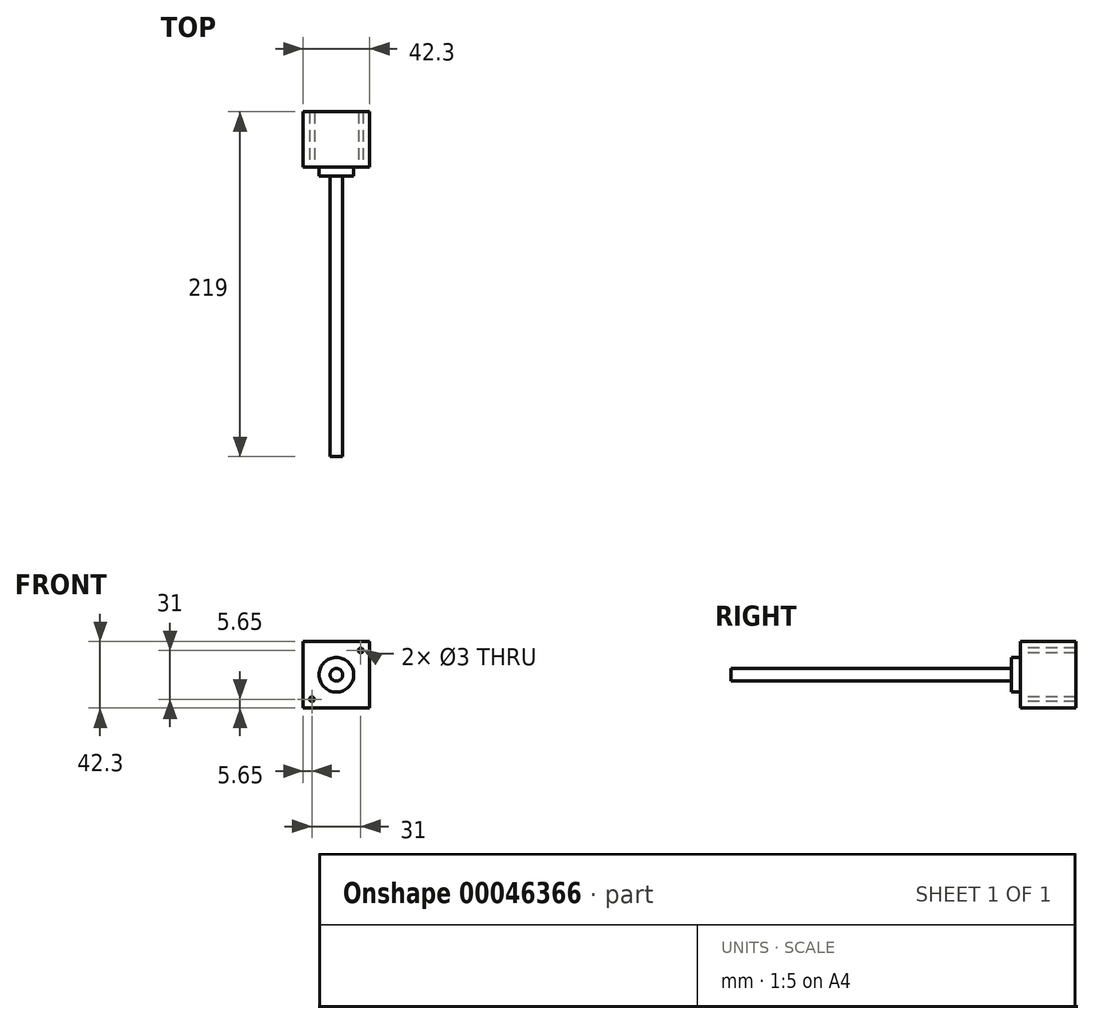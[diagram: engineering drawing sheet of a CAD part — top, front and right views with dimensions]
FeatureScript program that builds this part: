
annotation { "Feature Type Name" : "Feature", "Feature Type Description" : "" }
export const myFeature = defineFeature(function(context is Context, id is Id, definition is map)
    precondition{}
    {
        {
            var Q0;
            Q0=qCreatedBy(makeId("Front.planeOp"),FACE);
            var sketch = newSketch(context, id + "F0", { "sketchPlane" : qUnion([Q0])});
            skLineSegment(sketch, "E0.bottom", {"start": v(0, 0) * mm, "end": v(42.3, 0) * mm});
            skLineSegment(sketch, "E0.top", {"start": v(0, 42.3) * mm, "end": v(42.3, 42.3) * mm});
            skLineSegment(sketch, "E0.left", {"start": v(0, 0) * mm, "end": v(0, 42.3) * mm});
            skLineSegment(sketch, "E0.right", {"start": v(42.3, 0) * mm, "end": v(42.3, 42.3) * mm});
            skLineSegment(sketch, "E1", {"start": v(0, 21.15) * mm, "end": v(42.3, 21.15) * mm, "construction": true});
            skLineSegment(sketch, "E2", {"start": v(21.15, 42.3) * mm, "end": v(21.15, 0) * mm, "construction": true});
            skCircle(sketch, "E3", {"center": v(21.15, 21.15) * mm, "radius": 11 * mm});
            skCircle(sketch, "E4", {"center": v(5.65, 36.65) * mm, "radius": 1.5 * mm});
            skCircle(sketch, "E5.0.MirrorC", {"center": v(36.65, 36.65) * mm, "radius": 1.5 * mm});
            skCircle(sketch, "E6.0.MirrorC", {"center": v(5.65, 5.65) * mm, "radius": 1.5 * mm});
            skCircle(sketch, "E7.0.MirrorC", {"center": v(36.65, 5.65) * mm, "radius": 1.5 * mm});
            skCircle(sketch, "E8", {"center": v(21.15, 21.15) * mm, "radius": 4 * mm});
            skCircle(sketch, "E9", {"center": v(21.15, 21.15) * mm, "radius": 2.5 * mm});
            skSolve(sketch);
        }
        {
            var Q0;
            Q0=makeQuery(id+"F0.imprint","IMPRINT",FACE,{"disambiguationData":[TD([[makeQuery(id+"F0.imprint","IMPRINT",EDGE,{"derivedFrom":sQuery(id+"F0.wireOp",EDGE,"E0.bottom")}),1.0]])]});
            var Q1;
            Q1=makeQuery(id+"F0.imprint","IMPRINT",FACE,{"disambiguationData":[TD([[makeQuery(id+"F0.imprint","IMPRINT",EDGE,{"derivedFrom":sQuery(id+"F0.wireOp",EDGE,"E4")}),1.0]])]});
            var Q2;
            Q2=makeQuery(id+"F0.imprint","IMPRINT",FACE,{"disambiguationData":[TD([[makeQuery(id+"F0.imprint","IMPRINT",EDGE,{"derivedFrom":sQuery(id+"F0.wireOp",EDGE,"E5.0.MirrorC")}),-1.0]])]});
            var Q3;
            Q3=makeQuery(id+"F0.imprint","IMPRINT",FACE,{"disambiguationData":[TD([[makeQuery(id+"F0.imprint","IMPRINT",EDGE,{"derivedFrom":sQuery(id+"F0.wireOp",EDGE,"E3")}),1.0]])]});
            var Q4;
            Q4=makeQuery(id+"F0.imprint","IMPRINT",FACE,{"disambiguationData":[TD([[makeQuery(id+"F0.imprint","IMPRINT",EDGE,{"derivedFrom":sQuery(id+"F0.wireOp",EDGE,"E6.0.MirrorC")}),-1.0]])]});
            var Q5;
            Q5=makeQuery(id+"F0.imprint","IMPRINT",FACE,{"disambiguationData":[TD([[makeQuery(id+"F0.imprint","IMPRINT",EDGE,{"derivedFrom":sQuery(id+"F0.wireOp",EDGE,"E7.0.MirrorC")}),1.0]])]});
            var Q6;
            Q6=makeQuery(id+"F0.imprint","IMPRINT",FACE,{"disambiguationData":[TD([[makeQuery(id+"F0.imprint","IMPRINT",EDGE,{"derivedFrom":sQuery(id+"F0.wireOp",EDGE,"E8")}),1.0]])]});
            var Q7;
            Q7=makeQuery(id+"F0.imprint","IMPRINT",FACE,{"disambiguationData":[TD([[makeQuery(id+"F0.imprint","IMPRINT",EDGE,{"derivedFrom":sQuery(id+"F0.wireOp",EDGE,"E9")}),1.0]])]});
            extrude(context, id + "F1", {"entities" : qUnion([Q0, Q1, Q2, Q3, Q4, Q5, Q6, Q7]), "oppositeDirection" : true, "depth" : 39 * mm});
        }
        {
            var Q0;
            Q0=makeQuery(id+"F0.imprint","IMPRINT",FACE,{"disambiguationData":[TD([[makeQuery(id+"F0.imprint","IMPRINT",EDGE,{"derivedFrom":sQuery(id+"F0.wireOp",EDGE,"E3")}),1.0]])]});
            var Q1;
            Q1=makeQuery(id+"F0.imprint","IMPRINT",FACE,{"disambiguationData":[TD([[makeQuery(id+"F0.imprint","IMPRINT",EDGE,{"derivedFrom":sQuery(id+"F0.wireOp",EDGE,"E9")}),1.0]])]});
            var Q2;
            Q2=makeQuery(id+"F0.imprint","IMPRINT",FACE,{"disambiguationData":[TD([[makeQuery(id+"F0.imprint","IMPRINT",EDGE,{"derivedFrom":sQuery(id+"F0.wireOp",EDGE,"E8")}),1.0]])]});
            extrude(context, id + "F2", {"entities" : qUnion([Q0, Q1, Q2]), "operationType" : NewBodyOperationType.ADD, "depth" : 2 * mm});
        }
        {
            var Q0;
            Q0=makeQuery(id+"F0.imprint","IMPRINT",FACE,{"disambiguationData":[TD([[makeQuery(id+"F0.imprint","IMPRINT",EDGE,{"derivedFrom":sQuery(id+"F0.wireOp",EDGE,"E4")}),1.0]])]});
            var Q1;
            Q1=makeQuery(id+"F0.imprint","IMPRINT",FACE,{"disambiguationData":[TD([[makeQuery(id+"F0.imprint","IMPRINT",EDGE,{"derivedFrom":sQuery(id+"F0.wireOp",EDGE,"E5.0.MirrorC")}),-1.0]])]});
            var Q2;
            Q2=makeQuery(id+"F0.imprint","IMPRINT",FACE,{"disambiguationData":[TD([[makeQuery(id+"F0.imprint","IMPRINT",EDGE,{"derivedFrom":sQuery(id+"F0.wireOp",EDGE,"E7.0.MirrorC")}),1.0]])]});
            var Q3;
            Q3=makeQuery(id+"F0.imprint","IMPRINT",FACE,{"disambiguationData":[TD([[makeQuery(id+"F0.imprint","IMPRINT",EDGE,{"derivedFrom":sQuery(id+"F0.wireOp",EDGE,"E6.0.MirrorC")}),-1.0]])]});
            extrude(context, id + "F3", {"entities" : qUnion([Q0, Q1, Q2, Q3]), "operationType" : NewBodyOperationType.REMOVE, "oppositeDirection" : true, "depth" : 4 * mm});
        }
        {
            var Q0;
            Q0=makeQuery(id+"F1.opExtrude","SWEPT_BODY",BODY,{"disambiguationData":[OSD([sQuery(id+"F0.wireOp",EDGE,"E0.bottom"),sQuery(id+"F0.wireOp",EDGE,"E0.top"),sQuery(id+"F0.wireOp",EDGE,"E0.left"),sQuery(id+"F0.wireOp",EDGE,"E0.right")])]});
            transform(context, id + "F4", {"entities" : qUnion([Q0]), "transformType" : TransformType.COPY});
        }
        {
            var Q0;
            Q0=makeQuery(id+"F0.imprint","IMPRINT",FACE,{"disambiguationData":[TD([[makeQuery(id+"F0.imprint","IMPRINT",EDGE,{"derivedFrom":sQuery(id+"F0.wireOp",EDGE,"E8")}),1.0]])]});
            var Q1;
            Q1=makeQuery(id+"F0.imprint","IMPRINT",FACE,{"disambiguationData":[TD([[makeQuery(id+"F0.imprint","IMPRINT",EDGE,{"derivedFrom":sQuery(id+"F0.wireOp",EDGE,"E9")}),1.0]])]});
            extrude(context, id + "F5", {"entities" : qUnion([Q0, Q1]), "operationType" : NewBodyOperationType.ADD, "depth" : 180 * mm});
        }
        {
            var Q0;
            Q0=makeQuery(id+"F0.imprint","IMPRINT",FACE,{"disambiguationData":[TD([[makeQuery(id+"F0.imprint","IMPRINT",EDGE,{"derivedFrom":sQuery(id+"F0.wireOp",EDGE,"E9")}),1.0]])]});
            extrude(context, id + "F6", {"entities" : qUnion([Q0]), "operationType" : NewBodyOperationType.ADD, "depth" : 24 * mm});
        }
    });
